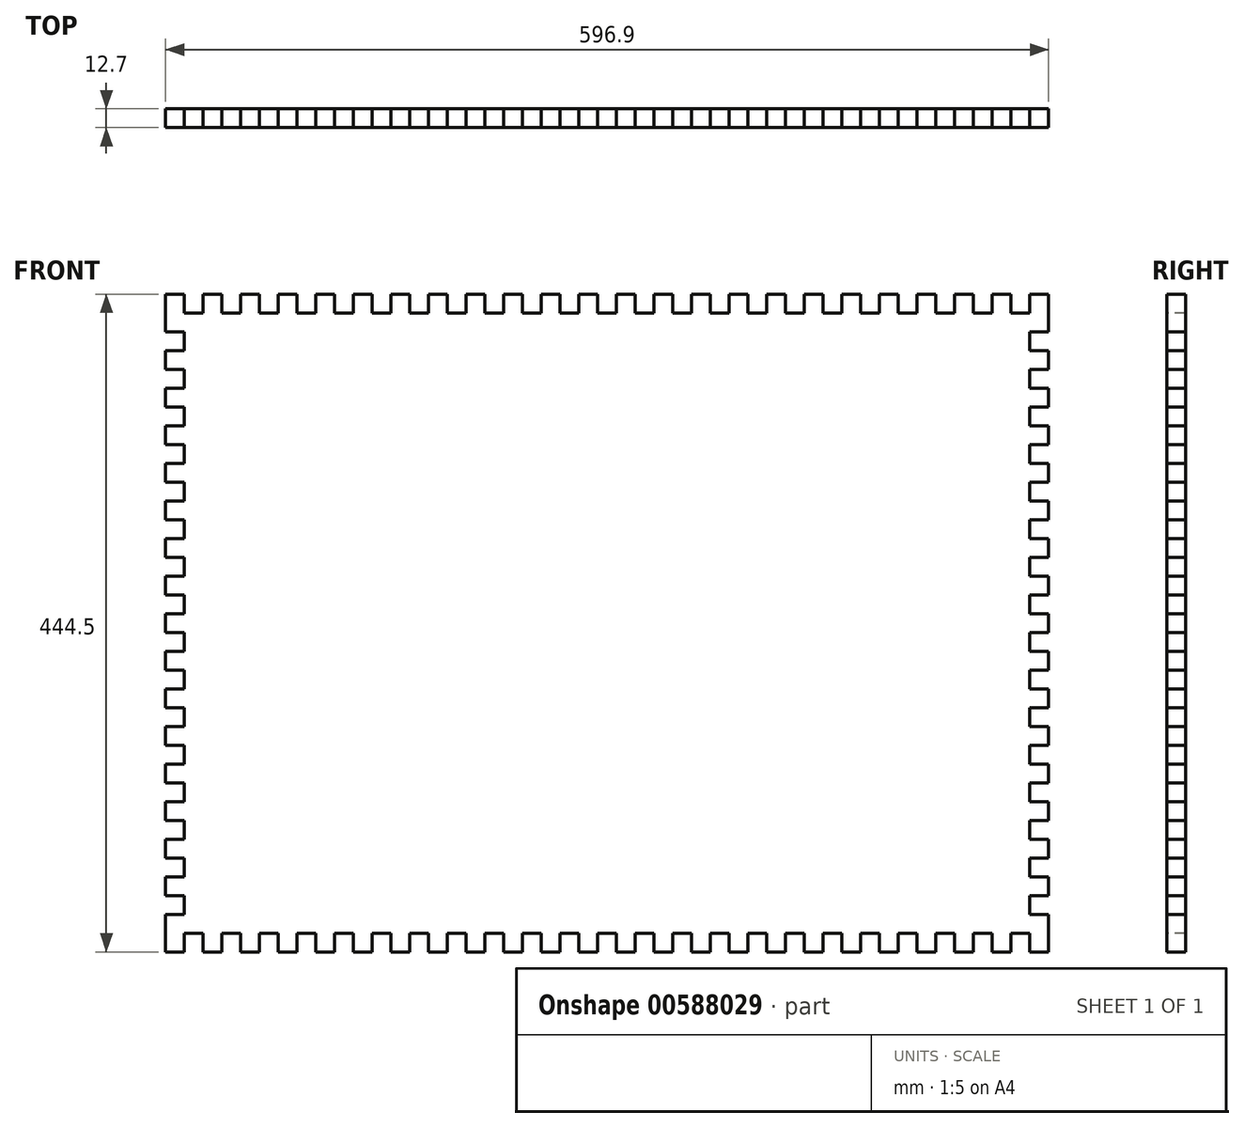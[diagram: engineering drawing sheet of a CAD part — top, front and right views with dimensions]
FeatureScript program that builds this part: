
annotation { "Feature Type Name" : "Feature", "Feature Type Description" : "" }
export const myFeature = defineFeature(function(context is Context, id is Id, definition is map)
    precondition{}
    {
        {
            var Q0;
            Q0=qCreatedBy(makeId("Front.planeOp"),FACE);
            var sketch = newSketch(context, id + "F0", { "sketchPlane" : qUnion([Q0])});
            skLineSegment(sketch, "E0", {"start": v(12.7, 12.7) * mm, "end": v(25.4, 12.7) * mm});
            skLineSegment(sketch, "E1.MirrorCS", {"start": v(12.7, 0) * mm, "end": v(12.7, 12.7) * mm});
            skLineSegment(sketch, "E2.MirrorCS", {"start": v(0, 0) * mm, "end": v(12.7, 0) * mm});
            skLineSegment(sketch, "E3.1.0.0", {"start": v(25.4, 0) * mm, "end": v(38.1, 0) * mm});
            skLineSegment(sketch, "E3.1.0.1", {"start": v(25.4, 12.7) * mm, "end": v(25.4, 0) * mm});
            skLineSegment(sketch, "E3.1.0.2", {"start": v(38.1, 0) * mm, "end": v(38.1, 12.7) * mm});
            skLineSegment(sketch, "E3.1.0.3", {"start": v(38.1, 12.7) * mm, "end": v(50.8, 12.7) * mm});
            skLineSegment(sketch, "E3.2.0.0", {"start": v(50.8, 0) * mm, "end": v(63.5, 0) * mm});
            skLineSegment(sketch, "E3.2.0.1", {"start": v(50.8, 12.7) * mm, "end": v(50.8, 0) * mm});
            skLineSegment(sketch, "E3.2.0.2", {"start": v(63.5, 0) * mm, "end": v(63.5, 12.7) * mm});
            skLineSegment(sketch, "E3.2.0.3", {"start": v(63.5, 12.7) * mm, "end": v(76.2, 12.7) * mm});
            skLineSegment(sketch, "E3.3.0.0", {"start": v(76.2, 0) * mm, "end": v(88.9, 0) * mm});
            skLineSegment(sketch, "E3.3.0.1", {"start": v(76.2, 12.7) * mm, "end": v(76.2, 0) * mm});
            skLineSegment(sketch, "E3.3.0.2", {"start": v(88.9, 0) * mm, "end": v(88.9, 12.7) * mm});
            skLineSegment(sketch, "E3.3.0.3", {"start": v(88.9, 12.7) * mm, "end": v(101.6, 12.7) * mm});
            skLineSegment(sketch, "E3.4.0.0", {"start": v(101.6, 0) * mm, "end": v(114.3, 0) * mm});
            skLineSegment(sketch, "E3.4.0.1", {"start": v(101.6, 12.7) * mm, "end": v(101.6, 0) * mm});
            skLineSegment(sketch, "E3.4.0.2", {"start": v(114.3, 0) * mm, "end": v(114.3, 12.7) * mm});
            skLineSegment(sketch, "E3.4.0.3", {"start": v(114.3, 12.7) * mm, "end": v(127, 12.7) * mm});
            skLineSegment(sketch, "E3.5.0.0", {"start": v(127, 0) * mm, "end": v(139.7, 0) * mm});
            skLineSegment(sketch, "E3.5.0.1", {"start": v(127, 12.7) * mm, "end": v(127, 0) * mm});
            skLineSegment(sketch, "E3.5.0.2", {"start": v(139.7, 0) * mm, "end": v(139.7, 12.7) * mm});
            skLineSegment(sketch, "E3.5.0.3", {"start": v(139.7, 12.7) * mm, "end": v(152.4, 12.7) * mm});
            skLineSegment(sketch, "E3.6.0.0", {"start": v(152.4, 0) * mm, "end": v(165.1, 0) * mm});
            skLineSegment(sketch, "E3.6.0.1", {"start": v(152.4, 12.7) * mm, "end": v(152.4, 0) * mm});
            skLineSegment(sketch, "E3.6.0.2", {"start": v(165.1, 0) * mm, "end": v(165.1, 12.7) * mm});
            skLineSegment(sketch, "E3.6.0.3", {"start": v(165.1, 12.7) * mm, "end": v(177.8, 12.7) * mm});
            skLineSegment(sketch, "E3.7.0.0", {"start": v(177.8, 0) * mm, "end": v(190.5, 0) * mm});
            skLineSegment(sketch, "E3.7.0.1", {"start": v(177.8, 12.7) * mm, "end": v(177.8, 0) * mm});
            skLineSegment(sketch, "E3.7.0.2", {"start": v(190.5, 0) * mm, "end": v(190.5, 12.7) * mm});
            skLineSegment(sketch, "E3.7.0.3", {"start": v(190.5, 12.7) * mm, "end": v(203.2, 12.7) * mm});
            skLineSegment(sketch, "E3.8.0.0", {"start": v(203.2, 0) * mm, "end": v(215.9, 0) * mm});
            skLineSegment(sketch, "E3.8.0.1", {"start": v(203.2, 12.7) * mm, "end": v(203.2, 0) * mm});
            skLineSegment(sketch, "E3.8.0.2", {"start": v(215.9, 0) * mm, "end": v(215.9, 12.7) * mm});
            skLineSegment(sketch, "E3.8.0.3", {"start": v(215.9, 12.7) * mm, "end": v(228.6, 12.7) * mm});
            skLineSegment(sketch, "E3.9.0.0", {"start": v(228.6, 0) * mm, "end": v(241.3, 0) * mm});
            skLineSegment(sketch, "E3.9.0.1", {"start": v(228.6, 12.7) * mm, "end": v(228.6, 0) * mm});
            skLineSegment(sketch, "E3.9.0.2", {"start": v(241.3, 0) * mm, "end": v(241.3, 12.7) * mm});
            skLineSegment(sketch, "E3.9.0.3", {"start": v(241.3, 12.7) * mm, "end": v(254, 12.7) * mm});
            skLineSegment(sketch, "E3.10.0.0", {"start": v(254, 0) * mm, "end": v(266.7, 0) * mm});
            skLineSegment(sketch, "E3.10.0.1", {"start": v(254, 12.7) * mm, "end": v(254, 0) * mm});
            skLineSegment(sketch, "E3.10.0.2", {"start": v(266.7, 0) * mm, "end": v(266.7, 12.7) * mm});
            skLineSegment(sketch, "E3.10.0.3", {"start": v(266.7, 12.7) * mm, "end": v(279.4, 12.7) * mm});
            skLineSegment(sketch, "E3.11.0.0", {"start": v(279.4, 0) * mm, "end": v(292.1, 0) * mm});
            skLineSegment(sketch, "E3.11.0.1", {"start": v(279.4, 12.7) * mm, "end": v(279.4, 0) * mm});
            skLineSegment(sketch, "E3.11.0.2", {"start": v(292.1, 0) * mm, "end": v(292.1, 12.7) * mm});
            skLineSegment(sketch, "E3.11.0.3", {"start": v(292.1, 12.7) * mm, "end": v(304.8, 12.7) * mm});
            skLineSegment(sketch, "E3.12.0.0", {"start": v(304.8, 0) * mm, "end": v(317.5, 0) * mm});
            skLineSegment(sketch, "E3.12.0.1", {"start": v(304.8, 12.7) * mm, "end": v(304.8, 0) * mm});
            skLineSegment(sketch, "E3.12.0.2", {"start": v(317.5, 0) * mm, "end": v(317.5, 12.7) * mm});
            skLineSegment(sketch, "E3.12.0.3", {"start": v(317.5, 12.7) * mm, "end": v(330.2, 12.7) * mm});
            skLineSegment(sketch, "E3.13.0.0", {"start": v(330.2, 0) * mm, "end": v(342.9, 0) * mm});
            skLineSegment(sketch, "E3.13.0.1", {"start": v(330.2, 12.7) * mm, "end": v(330.2, 0) * mm});
            skLineSegment(sketch, "E3.13.0.2", {"start": v(342.9, 0) * mm, "end": v(342.9, 12.7) * mm});
            skLineSegment(sketch, "E3.13.0.3", {"start": v(342.9, 12.7) * mm, "end": v(355.6, 12.7) * mm});
            skLineSegment(sketch, "E3.14.0.0", {"start": v(355.6, 0) * mm, "end": v(368.3, 0) * mm});
            skLineSegment(sketch, "E3.14.0.1", {"start": v(355.6, 12.7) * mm, "end": v(355.6, 0) * mm});
            skLineSegment(sketch, "E3.14.0.2", {"start": v(368.3, 0) * mm, "end": v(368.3, 12.7) * mm});
            skLineSegment(sketch, "E3.14.0.3", {"start": v(368.3, 12.7) * mm, "end": v(381, 12.7) * mm});
            skLineSegment(sketch, "E3.15.0.0", {"start": v(381, 0) * mm, "end": v(393.7, 0) * mm});
            skLineSegment(sketch, "E3.15.0.1", {"start": v(381, 12.7) * mm, "end": v(381, 0) * mm});
            skLineSegment(sketch, "E3.15.0.2", {"start": v(393.7, 0) * mm, "end": v(393.7, 12.7) * mm});
            skLineSegment(sketch, "E3.15.0.3", {"start": v(393.7, 12.7) * mm, "end": v(406.4, 12.7) * mm});
            skLineSegment(sketch, "E3.16.0.0", {"start": v(406.4, 0) * mm, "end": v(419.1, 0) * mm});
            skLineSegment(sketch, "E3.16.0.1", {"start": v(406.4, 12.7) * mm, "end": v(406.4, 0) * mm});
            skLineSegment(sketch, "E3.16.0.2", {"start": v(419.1, 0) * mm, "end": v(419.1, 12.7) * mm});
            skLineSegment(sketch, "E3.16.0.3", {"start": v(419.1, 12.7) * mm, "end": v(431.8, 12.7) * mm});
            skLineSegment(sketch, "E3.17.0.0", {"start": v(431.8, 0) * mm, "end": v(444.5, 0) * mm});
            skLineSegment(sketch, "E3.17.0.1", {"start": v(431.8, 12.7) * mm, "end": v(431.8, 0) * mm});
            skLineSegment(sketch, "E3.17.0.2", {"start": v(444.5, 0) * mm, "end": v(444.5, 12.7) * mm});
            skLineSegment(sketch, "E3.17.0.3", {"start": v(444.5, 12.7) * mm, "end": v(457.2, 12.7) * mm});
            skLineSegment(sketch, "E3.18.0.0", {"start": v(457.2, 0) * mm, "end": v(469.9, 0) * mm});
            skLineSegment(sketch, "E3.18.0.1", {"start": v(457.2, 12.7) * mm, "end": v(457.2, 0) * mm});
            skLineSegment(sketch, "E3.18.0.2", {"start": v(469.9, 0) * mm, "end": v(469.9, 12.7) * mm});
            skLineSegment(sketch, "E3.18.0.3", {"start": v(469.9, 12.7) * mm, "end": v(482.6, 12.7) * mm});
            skLineSegment(sketch, "E3.19.0.0", {"start": v(482.6, 0) * mm, "end": v(495.3, 0) * mm});
            skLineSegment(sketch, "E3.19.0.1", {"start": v(482.6, 12.7) * mm, "end": v(482.6, 0) * mm});
            skLineSegment(sketch, "E3.19.0.2", {"start": v(495.3, 0) * mm, "end": v(495.3, 12.7) * mm});
            skLineSegment(sketch, "E3.19.0.3", {"start": v(495.3, 12.7) * mm, "end": v(508, 12.7) * mm});
            skLineSegment(sketch, "E3.20.0.0", {"start": v(508, 0) * mm, "end": v(520.7, 0) * mm});
            skLineSegment(sketch, "E3.20.0.1", {"start": v(508, 12.7) * mm, "end": v(508, 0) * mm});
            skLineSegment(sketch, "E3.20.0.2", {"start": v(520.7, 0) * mm, "end": v(520.7, 12.7) * mm});
            skLineSegment(sketch, "E3.20.0.3", {"start": v(520.7, 12.7) * mm, "end": v(533.4, 12.7) * mm});
            skLineSegment(sketch, "E3.21.0.0", {"start": v(533.4, 0) * mm, "end": v(546.1, 0) * mm});
            skLineSegment(sketch, "E3.21.0.1", {"start": v(533.4, 12.7) * mm, "end": v(533.4, 0) * mm});
            skLineSegment(sketch, "E3.21.0.2", {"start": v(546.1, 0) * mm, "end": v(546.1, 12.7) * mm});
            skLineSegment(sketch, "E3.21.0.3", {"start": v(546.1, 12.7) * mm, "end": v(558.8, 12.7) * mm});
            skLineSegment(sketch, "E3.22.0.0", {"start": v(558.8, 0) * mm, "end": v(571.5, 0) * mm});
            skLineSegment(sketch, "E3.22.0.1", {"start": v(558.8, 12.7) * mm, "end": v(558.8, 0) * mm});
            skLineSegment(sketch, "E3.22.0.2", {"start": v(571.5, 0) * mm, "end": v(571.5, 12.7) * mm});
            skLineSegment(sketch, "E3.22.0.3", {"start": v(571.5, 12.7) * mm, "end": v(584.2, 12.7) * mm});
            skLineSegment(sketch, "E3.23.0.1", {"start": v(584.2, 12.7) * mm, "end": v(584.2, 0) * mm});
            skLineSegment(sketch, "E4", {"start": v(571.5, 431.8) * mm, "end": v(571.5, 444.5) * mm});
            skLineSegment(sketch, "E5.1.0.0", {"start": v(571.5, 444.5) * mm, "end": v(558.8, 444.5) * mm});
            skLineSegment(sketch, "E5.1.0.1", {"start": v(558.8, 444.5) * mm, "end": v(558.8, 431.8) * mm});
            skLineSegment(sketch, "E5.1.0.2", {"start": v(558.8, 431.8) * mm, "end": v(546.1, 431.8) * mm});
            skLineSegment(sketch, "E5.1.0.3", {"start": v(546.1, 431.8) * mm, "end": v(546.1, 444.5) * mm});
            skLineSegment(sketch, "E5.2.0.0", {"start": v(546.1, 444.5) * mm, "end": v(533.4, 444.5) * mm});
            skLineSegment(sketch, "E5.2.0.1", {"start": v(533.4, 444.5) * mm, "end": v(533.4, 431.8) * mm});
            skLineSegment(sketch, "E5.2.0.2", {"start": v(533.4, 431.8) * mm, "end": v(520.7, 431.8) * mm});
            skLineSegment(sketch, "E5.2.0.3", {"start": v(520.7, 431.8) * mm, "end": v(520.7, 444.5) * mm});
            skLineSegment(sketch, "E5.3.0.0", {"start": v(520.7, 444.5) * mm, "end": v(508, 444.5) * mm});
            skLineSegment(sketch, "E5.3.0.1", {"start": v(508, 444.5) * mm, "end": v(508, 431.8) * mm});
            skLineSegment(sketch, "E5.3.0.2", {"start": v(508, 431.8) * mm, "end": v(495.3, 431.8) * mm});
            skLineSegment(sketch, "E5.3.0.3", {"start": v(495.3, 431.8) * mm, "end": v(495.3, 444.5) * mm});
            skLineSegment(sketch, "E5.4.0.0", {"start": v(495.3, 444.5) * mm, "end": v(482.6, 444.5) * mm});
            skLineSegment(sketch, "E5.4.0.1", {"start": v(482.6, 444.5) * mm, "end": v(482.6, 431.8) * mm});
            skLineSegment(sketch, "E5.4.0.2", {"start": v(482.6, 431.8) * mm, "end": v(469.9, 431.8) * mm});
            skLineSegment(sketch, "E5.4.0.3", {"start": v(469.9, 431.8) * mm, "end": v(469.9, 444.5) * mm});
            skLineSegment(sketch, "E5.5.0.0", {"start": v(469.9, 444.5) * mm, "end": v(457.2, 444.5) * mm});
            skLineSegment(sketch, "E5.5.0.1", {"start": v(457.2, 444.5) * mm, "end": v(457.2, 431.8) * mm});
            skLineSegment(sketch, "E5.5.0.2", {"start": v(457.2, 431.8) * mm, "end": v(444.5, 431.8) * mm});
            skLineSegment(sketch, "E5.5.0.3", {"start": v(444.5, 431.8) * mm, "end": v(444.5, 444.5) * mm});
            skLineSegment(sketch, "E5.6.0.0", {"start": v(444.5, 444.5) * mm, "end": v(431.8, 444.5) * mm});
            skLineSegment(sketch, "E5.6.0.1", {"start": v(431.8, 444.5) * mm, "end": v(431.8, 431.8) * mm});
            skLineSegment(sketch, "E5.6.0.2", {"start": v(431.8, 431.8) * mm, "end": v(419.1, 431.8) * mm});
            skLineSegment(sketch, "E5.6.0.3", {"start": v(419.1, 431.8) * mm, "end": v(419.1, 444.5) * mm});
            skLineSegment(sketch, "E5.7.0.0", {"start": v(419.1, 444.5) * mm, "end": v(406.4, 444.5) * mm});
            skLineSegment(sketch, "E5.7.0.1", {"start": v(406.4, 444.5) * mm, "end": v(406.4, 431.8) * mm});
            skLineSegment(sketch, "E5.7.0.2", {"start": v(406.4, 431.8) * mm, "end": v(393.7, 431.8) * mm});
            skLineSegment(sketch, "E5.7.0.3", {"start": v(393.7, 431.8) * mm, "end": v(393.7, 444.5) * mm});
            skLineSegment(sketch, "E5.8.0.0", {"start": v(393.7, 444.5) * mm, "end": v(381, 444.5) * mm});
            skLineSegment(sketch, "E5.8.0.1", {"start": v(381, 444.5) * mm, "end": v(381, 431.8) * mm});
            skLineSegment(sketch, "E5.8.0.2", {"start": v(381, 431.8) * mm, "end": v(368.3, 431.8) * mm});
            skLineSegment(sketch, "E5.8.0.3", {"start": v(368.3, 431.8) * mm, "end": v(368.3, 444.5) * mm});
            skLineSegment(sketch, "E5.9.0.0", {"start": v(368.3, 444.5) * mm, "end": v(355.6, 444.5) * mm});
            skLineSegment(sketch, "E5.9.0.1", {"start": v(355.6, 444.5) * mm, "end": v(355.6, 431.8) * mm});
            skLineSegment(sketch, "E5.9.0.2", {"start": v(355.6, 431.8) * mm, "end": v(342.9, 431.8) * mm});
            skLineSegment(sketch, "E5.9.0.3", {"start": v(342.9, 431.8) * mm, "end": v(342.9, 444.5) * mm});
            skLineSegment(sketch, "E5.10.0.0", {"start": v(342.9, 444.5) * mm, "end": v(330.2, 444.5) * mm});
            skLineSegment(sketch, "E5.10.0.1", {"start": v(330.2, 444.5) * mm, "end": v(330.2, 431.8) * mm});
            skLineSegment(sketch, "E5.10.0.2", {"start": v(330.2, 431.8) * mm, "end": v(317.5, 431.8) * mm});
            skLineSegment(sketch, "E5.10.0.3", {"start": v(317.5, 431.8) * mm, "end": v(317.5, 444.5) * mm});
            skLineSegment(sketch, "E5.11.0.0", {"start": v(317.5, 444.5) * mm, "end": v(304.8, 444.5) * mm});
            skLineSegment(sketch, "E5.11.0.1", {"start": v(304.8, 444.5) * mm, "end": v(304.8, 431.8) * mm});
            skLineSegment(sketch, "E5.11.0.2", {"start": v(304.8, 431.8) * mm, "end": v(292.1, 431.8) * mm});
            skLineSegment(sketch, "E5.11.0.3", {"start": v(292.1, 431.8) * mm, "end": v(292.1, 444.5) * mm});
            skLineSegment(sketch, "E5.12.0.0", {"start": v(292.1, 444.5) * mm, "end": v(279.4, 444.5) * mm});
            skLineSegment(sketch, "E5.12.0.1", {"start": v(279.4, 444.5) * mm, "end": v(279.4, 431.8) * mm});
            skLineSegment(sketch, "E5.12.0.2", {"start": v(279.4, 431.8) * mm, "end": v(266.7, 431.8) * mm});
            skLineSegment(sketch, "E5.12.0.3", {"start": v(266.7, 431.8) * mm, "end": v(266.7, 444.5) * mm});
            skLineSegment(sketch, "E5.13.0.0", {"start": v(266.7, 444.5) * mm, "end": v(254, 444.5) * mm});
            skLineSegment(sketch, "E5.13.0.1", {"start": v(254, 444.5) * mm, "end": v(254, 431.8) * mm});
            skLineSegment(sketch, "E5.13.0.2", {"start": v(254, 431.8) * mm, "end": v(241.3, 431.8) * mm});
            skLineSegment(sketch, "E5.13.0.3", {"start": v(241.3, 431.8) * mm, "end": v(241.3, 444.5) * mm});
            skLineSegment(sketch, "E5.14.0.0", {"start": v(241.3, 444.5) * mm, "end": v(228.6, 444.5) * mm});
            skLineSegment(sketch, "E5.14.0.1", {"start": v(228.6, 444.5) * mm, "end": v(228.6, 431.8) * mm});
            skLineSegment(sketch, "E5.14.0.2", {"start": v(228.6, 431.8) * mm, "end": v(215.9, 431.8) * mm});
            skLineSegment(sketch, "E5.14.0.3", {"start": v(215.9, 431.8) * mm, "end": v(215.9, 444.5) * mm});
            skLineSegment(sketch, "E5.15.0.0", {"start": v(215.9, 444.5) * mm, "end": v(203.2, 444.5) * mm});
            skLineSegment(sketch, "E5.15.0.1", {"start": v(203.2, 444.5) * mm, "end": v(203.2, 431.8) * mm});
            skLineSegment(sketch, "E5.15.0.2", {"start": v(203.2, 431.8) * mm, "end": v(190.5, 431.8) * mm});
            skLineSegment(sketch, "E5.15.0.3", {"start": v(190.5, 431.8) * mm, "end": v(190.5, 444.5) * mm});
            skLineSegment(sketch, "E5.16.0.0", {"start": v(190.5, 444.5) * mm, "end": v(177.8, 444.5) * mm});
            skLineSegment(sketch, "E5.16.0.1", {"start": v(177.8, 444.5) * mm, "end": v(177.8, 431.8) * mm});
            skLineSegment(sketch, "E5.16.0.2", {"start": v(177.8, 431.8) * mm, "end": v(165.1, 431.8) * mm});
            skLineSegment(sketch, "E5.16.0.3", {"start": v(165.1, 431.8) * mm, "end": v(165.1, 444.5) * mm});
            skLineSegment(sketch, "E5.17.0.0", {"start": v(165.1, 444.5) * mm, "end": v(152.4, 444.5) * mm});
            skLineSegment(sketch, "E5.17.0.1", {"start": v(152.4, 444.5) * mm, "end": v(152.4, 431.8) * mm});
            skLineSegment(sketch, "E5.17.0.2", {"start": v(152.4, 431.8) * mm, "end": v(139.7, 431.8) * mm});
            skLineSegment(sketch, "E5.17.0.3", {"start": v(139.7, 431.8) * mm, "end": v(139.7, 444.5) * mm});
            skLineSegment(sketch, "E5.18.0.0", {"start": v(139.7, 444.5) * mm, "end": v(127, 444.5) * mm});
            skLineSegment(sketch, "E5.18.0.1", {"start": v(127, 444.5) * mm, "end": v(127, 431.8) * mm});
            skLineSegment(sketch, "E5.18.0.2", {"start": v(127, 431.8) * mm, "end": v(114.3, 431.8) * mm});
            skLineSegment(sketch, "E5.18.0.3", {"start": v(114.3, 431.8) * mm, "end": v(114.3, 444.5) * mm});
            skLineSegment(sketch, "E5.19.0.0", {"start": v(114.3, 444.5) * mm, "end": v(101.6, 444.5) * mm});
            skLineSegment(sketch, "E5.19.0.1", {"start": v(101.6, 444.5) * mm, "end": v(101.6, 431.8) * mm});
            skLineSegment(sketch, "E5.19.0.2", {"start": v(101.6, 431.8) * mm, "end": v(88.9, 431.8) * mm});
            skLineSegment(sketch, "E5.19.0.3", {"start": v(88.9, 431.8) * mm, "end": v(88.9, 444.5) * mm});
            skLineSegment(sketch, "E5.20.0.0", {"start": v(88.9, 444.5) * mm, "end": v(76.2, 444.5) * mm});
            skLineSegment(sketch, "E5.20.0.1", {"start": v(76.2, 444.5) * mm, "end": v(76.2, 431.8) * mm});
            skLineSegment(sketch, "E5.20.0.2", {"start": v(76.2, 431.8) * mm, "end": v(63.5, 431.8) * mm});
            skLineSegment(sketch, "E5.20.0.3", {"start": v(63.5, 431.8) * mm, "end": v(63.5, 444.5) * mm});
            skLineSegment(sketch, "E5.21.0.0", {"start": v(63.5, 444.5) * mm, "end": v(50.8, 444.5) * mm});
            skLineSegment(sketch, "E5.21.0.1", {"start": v(50.8, 444.5) * mm, "end": v(50.8, 431.8) * mm});
            skLineSegment(sketch, "E5.21.0.2", {"start": v(50.8, 431.8) * mm, "end": v(38.1, 431.8) * mm});
            skLineSegment(sketch, "E5.21.0.3", {"start": v(38.1, 431.8) * mm, "end": v(38.1, 444.5) * mm});
            skLineSegment(sketch, "E5.22.0.0", {"start": v(38.1, 444.5) * mm, "end": v(25.4, 444.5) * mm});
            skLineSegment(sketch, "E5.22.0.1", {"start": v(25.4, 444.5) * mm, "end": v(25.4, 431.8) * mm});
            skLineSegment(sketch, "E5.22.0.2", {"start": v(25.4, 431.8) * mm, "end": v(12.7, 431.8) * mm});
            skLineSegment(sketch, "E6", {"start": v(0, 0) * mm, "end": v(0, 25.4) * mm});
            skLineSegment(sketch, "E7", {"start": v(0, 25.4) * mm, "end": v(12.7, 25.4) * mm});
            skLineSegment(sketch, "E8", {"start": v(12.7, 25.4) * mm, "end": v(12.7, 38.1) * mm});
            skLineSegment(sketch, "E9", {"start": v(12.7, 38.1) * mm, "end": v(0, 38.1) * mm});
            skLineSegment(sketch, "E10", {"start": v(0, 38.1) * mm, "end": v(0, 50.8) * mm});
            skLineSegment(sketch, "E11.0.1.0", {"start": v(0, 50.8) * mm, "end": v(12.7, 50.8) * mm});
            skLineSegment(sketch, "E11.0.1.1", {"start": v(12.7, 50.8) * mm, "end": v(12.7, 63.5) * mm});
            skLineSegment(sketch, "E11.0.1.2", {"start": v(12.7, 63.5) * mm, "end": v(0, 63.5) * mm});
            skLineSegment(sketch, "E11.0.1.3", {"start": v(0, 63.5) * mm, "end": v(0, 76.2) * mm});
            skLineSegment(sketch, "E11.0.2.0", {"start": v(0, 76.2) * mm, "end": v(12.7, 76.2) * mm});
            skLineSegment(sketch, "E11.0.2.1", {"start": v(12.7, 76.2) * mm, "end": v(12.7, 88.9) * mm});
            skLineSegment(sketch, "E11.0.2.2", {"start": v(12.7, 88.9) * mm, "end": v(0, 88.9) * mm});
            skLineSegment(sketch, "E11.0.2.3", {"start": v(0, 88.9) * mm, "end": v(0, 101.6) * mm});
            skLineSegment(sketch, "E11.0.3.0", {"start": v(0, 101.6) * mm, "end": v(12.7, 101.6) * mm});
            skLineSegment(sketch, "E11.0.3.1", {"start": v(12.7, 101.6) * mm, "end": v(12.7, 114.3) * mm});
            skLineSegment(sketch, "E11.0.3.2", {"start": v(12.7, 114.3) * mm, "end": v(0, 114.3) * mm});
            skLineSegment(sketch, "E11.0.3.3", {"start": v(0, 114.3) * mm, "end": v(0, 127) * mm});
            skLineSegment(sketch, "E11.0.4.0", {"start": v(0, 127) * mm, "end": v(12.7, 127) * mm});
            skLineSegment(sketch, "E11.0.4.1", {"start": v(12.7, 127) * mm, "end": v(12.7, 139.7) * mm});
            skLineSegment(sketch, "E11.0.4.2", {"start": v(12.7, 139.7) * mm, "end": v(0, 139.7) * mm});
            skLineSegment(sketch, "E11.0.4.3", {"start": v(0, 139.7) * mm, "end": v(0, 152.4) * mm});
            skLineSegment(sketch, "E11.0.5.0", {"start": v(0, 152.4) * mm, "end": v(12.7, 152.4) * mm});
            skLineSegment(sketch, "E11.0.5.1", {"start": v(12.7, 152.4) * mm, "end": v(12.7, 165.1) * mm});
            skLineSegment(sketch, "E11.0.5.2", {"start": v(12.7, 165.1) * mm, "end": v(0, 165.1) * mm});
            skLineSegment(sketch, "E11.0.5.3", {"start": v(0, 165.1) * mm, "end": v(0, 177.8) * mm});
            skLineSegment(sketch, "E11.0.6.0", {"start": v(0, 177.8) * mm, "end": v(12.7, 177.8) * mm});
            skLineSegment(sketch, "E11.0.6.1", {"start": v(12.7, 177.8) * mm, "end": v(12.7, 190.5) * mm});
            skLineSegment(sketch, "E11.0.6.2", {"start": v(12.7, 190.5) * mm, "end": v(0, 190.5) * mm});
            skLineSegment(sketch, "E11.0.6.3", {"start": v(0, 190.5) * mm, "end": v(0, 203.2) * mm});
            skLineSegment(sketch, "E11.0.7.0", {"start": v(0, 203.2) * mm, "end": v(12.7, 203.2) * mm});
            skLineSegment(sketch, "E11.0.7.1", {"start": v(12.7, 203.2) * mm, "end": v(12.7, 215.9) * mm});
            skLineSegment(sketch, "E11.0.7.2", {"start": v(12.7, 215.9) * mm, "end": v(0, 215.9) * mm});
            skLineSegment(sketch, "E11.0.7.3", {"start": v(0, 215.9) * mm, "end": v(0, 228.6) * mm});
            skLineSegment(sketch, "E11.0.8.0", {"start": v(0, 228.6) * mm, "end": v(12.7, 228.6) * mm});
            skLineSegment(sketch, "E11.0.8.1", {"start": v(12.7, 228.6) * mm, "end": v(12.7, 241.3) * mm});
            skLineSegment(sketch, "E11.0.8.2", {"start": v(12.7, 241.3) * mm, "end": v(0, 241.3) * mm});
            skLineSegment(sketch, "E11.0.8.3", {"start": v(0, 241.3) * mm, "end": v(0, 254) * mm});
            skLineSegment(sketch, "E11.0.9.0", {"start": v(0, 254) * mm, "end": v(12.7, 254) * mm});
            skLineSegment(sketch, "E11.0.9.1", {"start": v(12.7, 254) * mm, "end": v(12.7, 266.7) * mm});
            skLineSegment(sketch, "E11.0.9.2", {"start": v(12.7, 266.7) * mm, "end": v(0, 266.7) * mm});
            skLineSegment(sketch, "E11.0.9.3", {"start": v(0, 266.7) * mm, "end": v(0, 279.4) * mm});
            skLineSegment(sketch, "E11.0.10.0", {"start": v(0, 279.4) * mm, "end": v(12.7, 279.4) * mm});
            skLineSegment(sketch, "E11.0.10.1", {"start": v(12.7, 279.4) * mm, "end": v(12.7, 292.1) * mm});
            skLineSegment(sketch, "E11.0.10.2", {"start": v(12.7, 292.1) * mm, "end": v(0, 292.1) * mm});
            skLineSegment(sketch, "E11.0.10.3", {"start": v(0, 292.1) * mm, "end": v(0, 304.8) * mm});
            skLineSegment(sketch, "E11.0.11.0", {"start": v(0, 304.8) * mm, "end": v(12.7, 304.8) * mm});
            skLineSegment(sketch, "E11.0.11.1", {"start": v(12.7, 304.8) * mm, "end": v(12.7, 317.5) * mm});
            skLineSegment(sketch, "E11.0.11.2", {"start": v(12.7, 317.5) * mm, "end": v(0, 317.5) * mm});
            skLineSegment(sketch, "E11.0.11.3", {"start": v(0, 317.5) * mm, "end": v(0, 330.2) * mm});
            skLineSegment(sketch, "E11.0.12.0", {"start": v(0, 330.2) * mm, "end": v(12.7, 330.2) * mm});
            skLineSegment(sketch, "E11.0.12.1", {"start": v(12.7, 330.2) * mm, "end": v(12.7, 342.9) * mm});
            skLineSegment(sketch, "E11.0.12.2", {"start": v(12.7, 342.9) * mm, "end": v(0, 342.9) * mm});
            skLineSegment(sketch, "E11.0.12.3", {"start": v(0, 342.9) * mm, "end": v(0, 355.6) * mm});
            skLineSegment(sketch, "E11.0.13.0", {"start": v(0, 355.6) * mm, "end": v(12.7, 355.6) * mm});
            skLineSegment(sketch, "E11.0.13.1", {"start": v(12.7, 355.6) * mm, "end": v(12.7, 368.3) * mm});
            skLineSegment(sketch, "E11.0.13.2", {"start": v(12.7, 368.3) * mm, "end": v(0, 368.3) * mm});
            skLineSegment(sketch, "E11.0.13.3", {"start": v(0, 368.3) * mm, "end": v(0, 381) * mm});
            skLineSegment(sketch, "E11.0.14.0", {"start": v(0, 381) * mm, "end": v(12.7, 381) * mm});
            skLineSegment(sketch, "E11.0.14.1", {"start": v(12.7, 381) * mm, "end": v(12.7, 393.7) * mm});
            skLineSegment(sketch, "E11.0.14.2", {"start": v(12.7, 393.7) * mm, "end": v(0, 393.7) * mm});
            skLineSegment(sketch, "E11.0.14.3", {"start": v(0, 393.7) * mm, "end": v(0, 406.4) * mm});
            skLineSegment(sketch, "E11.0.15.0", {"start": v(0, 406.4) * mm, "end": v(12.7, 406.4) * mm});
            skLineSegment(sketch, "E11.0.15.1", {"start": v(12.7, 406.4) * mm, "end": v(12.7, 419.1) * mm});
            skLineSegment(sketch, "E11.0.15.2", {"start": v(12.7, 419.1) * mm, "end": v(0, 419.1) * mm});
            skLineSegment(sketch, "E12.1.0.1", {"start": v(596.9, 190.5) * mm, "end": v(596.9, 203.2) * mm});
            skLineSegment(sketch, "E12.1.0.2", {"start": v(596.9, 88.9) * mm, "end": v(596.9, 101.6) * mm});
            skLineSegment(sketch, "E12.1.0.4", {"start": v(596.9, 292.1) * mm, "end": v(596.9, 304.8) * mm});
            skLineSegment(sketch, "E12.1.0.22", {"start": v(596.9, 215.9) * mm, "end": v(596.9, 228.6) * mm});
            skLineSegment(sketch, "E12.1.0.23", {"start": v(596.9, 317.5) * mm, "end": v(596.9, 330.2) * mm});
            skLineSegment(sketch, "E12.1.0.25", {"start": v(596.9, 114.3) * mm, "end": v(596.9, 127) * mm});
            skLineSegment(sketch, "E12.1.0.29", {"start": v(596.9, 139.7) * mm, "end": v(596.9, 152.4) * mm});
            skLineSegment(sketch, "E12.1.0.30", {"start": v(596.9, 241.3) * mm, "end": v(596.9, 254) * mm});
            skLineSegment(sketch, "E12.1.0.31", {"start": v(596.9, 342.9) * mm, "end": v(596.9, 355.6) * mm});
            skLineSegment(sketch, "E12.1.0.32", {"start": v(596.9, 38.1) * mm, "end": v(596.9, 50.8) * mm});
            skLineSegment(sketch, "E12.1.0.45", {"start": v(596.9, 368.3) * mm, "end": v(596.9, 381) * mm});
            skLineSegment(sketch, "E12.1.0.58", {"start": v(596.9, 165.1) * mm, "end": v(596.9, 177.8) * mm});
            skLineSegment(sketch, "E12.1.0.63", {"start": v(596.9, 266.7) * mm, "end": v(596.9, 279.4) * mm});
            skLineSegment(sketch, "E12.1.0.64", {"start": v(596.9, 63.5) * mm, "end": v(596.9, 76.2) * mm});
            skLineSegment(sketch, "E13", {"start": v(584.2, 0) * mm, "end": v(596.9, 0) * mm});
            skLineSegment(sketch, "E14", {"start": v(596.9, 0) * mm, "end": v(596.9, 25.4) * mm});
            skLineSegment(sketch, "E15.MirrorCS", {"start": v(584.2, 101.6) * mm, "end": v(584.2, 114.3) * mm});
            skLineSegment(sketch, "E16.MirrorCS", {"start": v(584.2, 330.2) * mm, "end": v(584.2, 342.9) * mm});
            skLineSegment(sketch, "E17.MirrorCS", {"start": v(596.9, 330.2) * mm, "end": v(584.2, 330.2) * mm});
            skLineSegment(sketch, "E18.MirrorCS", {"start": v(584.2, 203.2) * mm, "end": v(584.2, 215.9) * mm});
            skLineSegment(sketch, "E19.MirrorCS", {"start": v(596.9, 76.2) * mm, "end": v(584.2, 76.2) * mm});
            skLineSegment(sketch, "E20.MirrorCS", {"start": v(596.9, 127) * mm, "end": v(584.2, 127) * mm});
            skLineSegment(sketch, "E21.MirrorCS", {"start": v(584.2, 228.6) * mm, "end": v(584.2, 241.3) * mm});
            skLineSegment(sketch, "E22.MirrorCS", {"start": v(584.2, 152.4) * mm, "end": v(584.2, 165.1) * mm});
            skLineSegment(sketch, "E23.MirrorCS", {"start": v(584.2, 50.8) * mm, "end": v(584.2, 63.5) * mm});
            skLineSegment(sketch, "E24.MirrorCS", {"start": v(596.9, 355.6) * mm, "end": v(584.2, 355.6) * mm});
            skLineSegment(sketch, "E25.MirrorCS", {"start": v(596.9, 101.6) * mm, "end": v(584.2, 101.6) * mm});
            skLineSegment(sketch, "E26.MirrorCS", {"start": v(584.2, 304.8) * mm, "end": v(584.2, 317.5) * mm});
            skLineSegment(sketch, "E27.MirrorCS", {"start": v(596.9, 203.2) * mm, "end": v(584.2, 203.2) * mm});
            skLineSegment(sketch, "E28.MirrorCS", {"start": v(596.9, 254) * mm, "end": v(584.2, 254) * mm});
            skLineSegment(sketch, "E29.MirrorCS", {"start": v(584.2, 279.4) * mm, "end": v(584.2, 292.1) * mm});
            skLineSegment(sketch, "E30.MirrorCS", {"start": v(584.2, 266.7) * mm, "end": v(596.9, 266.7) * mm});
            skLineSegment(sketch, "E31.MirrorCS", {"start": v(584.2, 254) * mm, "end": v(584.2, 266.7) * mm});
            skLineSegment(sketch, "E32.MirrorCS", {"start": v(584.2, 355.6) * mm, "end": v(584.2, 368.3) * mm});
            skLineSegment(sketch, "E33.MirrorCS", {"start": v(584.2, 38.1) * mm, "end": v(596.9, 38.1) * mm});
            skLineSegment(sketch, "E34.MirrorCS", {"start": v(584.2, 25.4) * mm, "end": v(584.2, 38.1) * mm});
            skLineSegment(sketch, "E35.MirrorCS", {"start": v(584.2, 127) * mm, "end": v(584.2, 139.7) * mm});
            skLineSegment(sketch, "E36.MirrorCS", {"start": v(596.9, 50.8) * mm, "end": v(584.2, 50.8) * mm});
            skLineSegment(sketch, "E37.MirrorCS", {"start": v(584.2, 190.5) * mm, "end": v(596.9, 190.5) * mm});
            skLineSegment(sketch, "E38.MirrorCS", {"start": v(584.2, 114.3) * mm, "end": v(596.9, 114.3) * mm});
            skLineSegment(sketch, "E39.MirrorCS", {"start": v(584.2, 215.9) * mm, "end": v(596.9, 215.9) * mm});
            skLineSegment(sketch, "E40.MirrorCS", {"start": v(584.2, 241.3) * mm, "end": v(596.9, 241.3) * mm});
            skLineSegment(sketch, "E41.MirrorCS", {"start": v(596.9, 304.8) * mm, "end": v(584.2, 304.8) * mm});
            skLineSegment(sketch, "E42.MirrorCS", {"start": v(584.2, 165.1) * mm, "end": v(596.9, 165.1) * mm});
            skLineSegment(sketch, "E43.MirrorCS", {"start": v(596.9, 228.6) * mm, "end": v(584.2, 228.6) * mm});
            skLineSegment(sketch, "E44.MirrorCS", {"start": v(584.2, 76.2) * mm, "end": v(584.2, 88.9) * mm});
            skLineSegment(sketch, "E45.MirrorCS", {"start": v(596.9, 25.4) * mm, "end": v(584.2, 25.4) * mm});
            skLineSegment(sketch, "E46.MirrorCS", {"start": v(584.2, 139.7) * mm, "end": v(596.9, 139.7) * mm});
            skLineSegment(sketch, "E47.MirrorCS", {"start": v(596.9, 152.4) * mm, "end": v(584.2, 152.4) * mm});
            skLineSegment(sketch, "E48.MirrorCS", {"start": v(584.2, 368.3) * mm, "end": v(596.9, 368.3) * mm});
            skLineSegment(sketch, "E49.MirrorCS", {"start": v(584.2, 63.5) * mm, "end": v(596.9, 63.5) * mm});
            skLineSegment(sketch, "E50.MirrorCS", {"start": v(584.2, 292.1) * mm, "end": v(596.9, 292.1) * mm});
            skLineSegment(sketch, "E51.MirrorCS", {"start": v(584.2, 88.9) * mm, "end": v(596.9, 88.9) * mm});
            skLineSegment(sketch, "E52.MirrorCS", {"start": v(596.9, 279.4) * mm, "end": v(584.2, 279.4) * mm});
            skLineSegment(sketch, "E53.MirrorCS", {"start": v(584.2, 342.9) * mm, "end": v(596.9, 342.9) * mm});
            skLineSegment(sketch, "E54.MirrorCS", {"start": v(584.2, 177.8) * mm, "end": v(584.2, 190.5) * mm});
            skLineSegment(sketch, "E55.MirrorCS", {"start": v(584.2, 317.5) * mm, "end": v(596.9, 317.5) * mm});
            skLineSegment(sketch, "E56.MirrorCS", {"start": v(596.9, 177.8) * mm, "end": v(584.2, 177.8) * mm});
            skLineSegment(sketch, "E57", {"start": v(12.7, 431.8) * mm, "end": v(12.7, 444.5) * mm});
            skLineSegment(sketch, "E58", {"start": v(12.7, 444.5) * mm, "end": v(0, 444.5) * mm});
            skLineSegment(sketch, "E59", {"start": v(0, 444.5) * mm, "end": v(0, 419.1) * mm});
            skLineSegment(sketch, "E60", {"start": v(571.5, 431.8) * mm, "end": v(584.2, 431.8) * mm});
            skLineSegment(sketch, "E61", {"start": v(584.2, 431.8) * mm, "end": v(584.2, 444.5) * mm});
            skLineSegment(sketch, "E62", {"start": v(584.2, 444.5) * mm, "end": v(596.9, 444.5) * mm});
            skLineSegment(sketch, "E63", {"start": v(596.9, 444.5) * mm, "end": v(596.9, 419.1) * mm});
            skLineSegment(sketch, "E64", {"start": v(596.9, 419.1) * mm, "end": v(584.2, 419.1) * mm});
            skLineSegment(sketch, "E65", {"start": v(584.2, 419.1) * mm, "end": v(584.2, 406.4) * mm});
            skLineSegment(sketch, "E66", {"start": v(584.2, 406.4) * mm, "end": v(596.9, 406.4) * mm});
            skLineSegment(sketch, "E67", {"start": v(596.9, 406.4) * mm, "end": v(596.9, 393.7) * mm});
            skLineSegment(sketch, "E68", {"start": v(596.9, 393.7) * mm, "end": v(584.2, 393.7) * mm});
            skLineSegment(sketch, "E69", {"start": v(584.2, 393.7) * mm, "end": v(584.2, 381) * mm});
            skLineSegment(sketch, "E70", {"start": v(584.2, 381) * mm, "end": v(596.9, 381) * mm});
            skSolve(sketch);
        }
        {
            var Q0;
            Q0=makeQuery(id+"F0.imprint","IMPRINT",FACE,{"disambiguationData":[TD([[makeQuery(id+"F0.imprint","IMPRINT",EDGE,{"derivedFrom":sQuery(id+"F0.wireOp",EDGE,"E0")}),1.0]])]});
            extrude(context, id + "F1", {"entities" : qUnion([Q0]), "oppositeDirection" : true, "depth" : 12.7 * mm, "offsetDistance" : 25.4 * mm});
        }
    });
